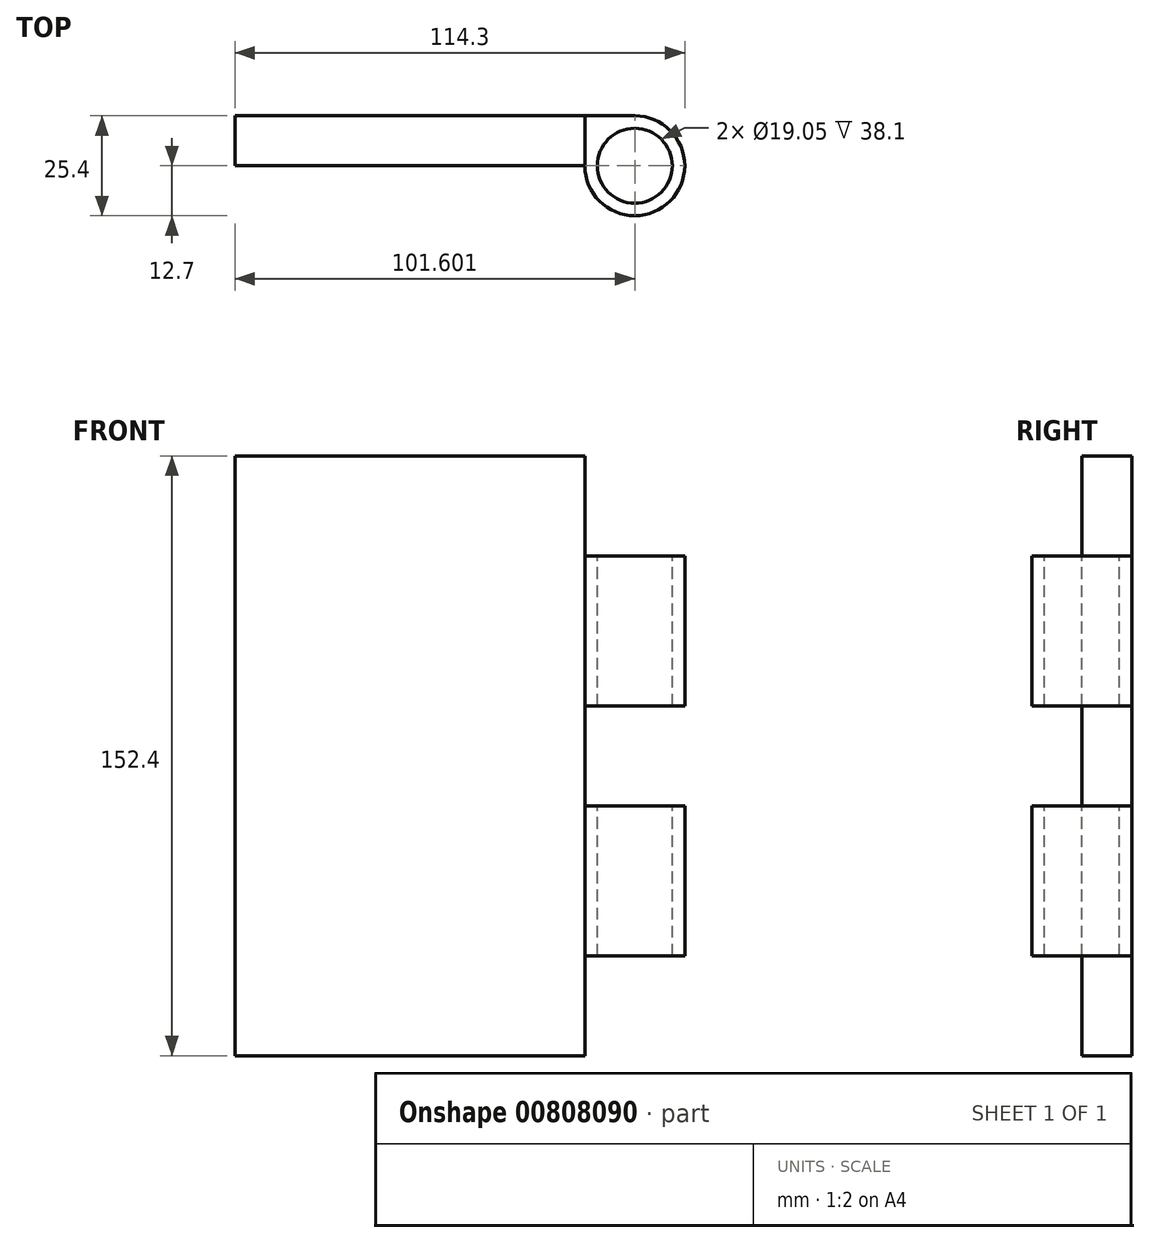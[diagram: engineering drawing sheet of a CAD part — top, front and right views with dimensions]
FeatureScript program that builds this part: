
annotation { "Feature Type Name" : "Feature", "Feature Type Description" : "" }
export const myFeature = defineFeature(function(context is Context, id is Id, definition is map)
    precondition{}
    {
        {
            var Q0;
            Q0=qCreatedBy(makeId("Front.planeOp"),FACE);
            var sketch = newSketch(context, id + "F0", { "sketchPlane" : qUnion([Q0])});
            skLineSegment(sketch, "E0.bottom", {"start": v(-39.5, 77.5) * mm, "end": v(62.1, 77.5) * mm});
            skLineSegment(sketch, "E0.top", {"start": v(-39.5, -74.9) * mm, "end": v(62.1, -74.9) * mm});
            skLineSegment(sketch, "E0.left", {"start": v(-39.5, 77.5) * mm, "end": v(-39.5, -74.9) * mm});
            skLineSegment(sketch, "E0.right", {"start": v(62.1, 77.5) * mm, "end": v(62.1, -74.9) * mm});
            skSolve(sketch);
        }
        {
            var Q0;
            Q0=makeQuery(id+"F0.imprint","IMPRINT",FACE,{"disambiguationData":[TD([[makeQuery(id+"F0.imprint","IMPRINT",EDGE,{"derivedFrom":sQuery(id+"F0.wireOp",EDGE,"E0.bottom")}),-1.0]])]});
            extrude(context, id + "F1", {"entities" : qUnion([Q0]), "depth" : 12.7 * mm, "offsetDistance" : 25.4 * mm});
        }
        {
            var Q0;
            Q0=makeQuery(id+"F1.opExtrude","SWEPT_FACE",FACE,{"disambiguationData":[OSD([sQuery(id+"F0.wireOp",EDGE,"E0.bottom")])]});
            var sketch = newSketch(context, id + "F2", { "sketchPlane" : qUnion([Q0])});
            skCircle(sketch, "E1", {"center": v(62.1, -12.7) * mm, "radius": 12.7 * mm});
            skSolve(sketch);
        }
        {
            var Q0;
            Q0=makeQuery(id+"F2.imprint","IMPRINT",FACE,{"disambiguationData":[TD([[makeQuery(id+"F2.imprint","IMPRINT",EDGE,{"derivedFrom":sQuery(id+"F2.wireOp",EDGE,"AtYBVnGq-jbLN-iIk4-UTEE-TkR76Q6qanXP")}),1.0]])]});
            var Q1;
            {var subQ1=sQuery(id+"F0.wireOp",EDGE,"E0.bottom");var subQ2=makeQuery(id+"F1.opExtrude","SWEPT_EDGE",EDGE,{"disambiguationData":[OSD([subQ1,sQuery(id+"F0.wireOp",EDGE,"E0.right")])]});Q1=makeQuery(id+"F2.imprint","IMPRINT",FACE,{"disambiguationData":[TD([[makeQuery(id+"F2.imprint","IMPRINT",EDGE,{"derivedFrom":subQ2}),-1.0]])]});}
            extrude(context, id + "F3", {"entities" : qUnion([Q0, Q1]), "operationType" : NewBodyOperationType.ADD, "oppositeDirection" : true, "depth" : 152.4 * mm, "offsetDistance" : 25.4 * mm});
        }
        {
            var Q0;
            {var subQ0=sQuery(id+"F0.wireOp",EDGE,"E0.bottom");Q0=makeQuery(id+"F3.boolean.opBoolean","MERGE",FACE,{"derivedFrom":[makeQuery(id+"F1.opExtrude","SWEPT_FACE",FACE,{"disambiguationData":[OSD([subQ0])]}),makeQuery(id+"F3.opExtrude","CAP_FACE",FACE,{"disambiguationData":[OSD([subQ0,sQuery(id+"F0.wireOp",EDGE,"E0.right"),sQuery(id+"F2.wireOp",EDGE,"AtYBVnGq-jbLN-iIk4-UTEE-TkR76Q6qanXP")])],"isStart":true})]});}
            var sketch = newSketch(context, id + "F4", { "sketchPlane" : qUnion([Q0])});
            skPoint(sketch, "E2", {"position": v(62.1, -12.7) * mm});
            skCircle(sketch, "E3", {"center": v(62.1, -12.7) * mm, "radius": 9.53 * mm});
            skSolve(sketch);
        }
        {
            var Q0;
            Q0=makeQuery(id+"F4.imprint","IMPRINT",FACE,{"disambiguationData":[TD([[makeQuery(id+"F4.imprint","IMPRINT",EDGE,{"derivedFrom":sQuery(id+"F4.wireOp",EDGE,"E3")}),1.0]])]});
            extrude(context, id + "F5", {"entities" : qUnion([Q0]), "operationType" : NewBodyOperationType.REMOVE, "endBound" : BoundingType.UP_TO_NEXT, "oppositeDirection" : true, "depth" : 25.4 * mm, "offsetDistance" : 25.4 * mm});
        }
        {
            var Q0;
            Q0=qCreatedBy(makeId("Front.planeOp"),FACE);
            cPlane(context, id + "F6", {"entities" : qUnion([Q0]), "cplaneType" : CPlaneType.OFFSET, "offset" : 25.4 * mm, "width" : 152.4 * mm, "height" : 152.4 * mm});
        }
        {
            var Q0;
            Q0=qCreatedBy(id+"F6.planeOp",FACE);
            var sketch = newSketch(context, id + "F7", { "sketchPlane" : qUnion([Q0])});
            skLineSegment(sketch, "E4.0", {"start": v(49.4, 77.5) * mm, "end": v(49.4, -74.9) * mm, "construction": true});
            skLineSegment(sketch, "E5.bottom", {"start": v(49.4, 77.5) * mm, "end": v(100.2, 77.5) * mm});
            skLineSegment(sketch, "E5.top", {"start": v(49.4, 52.1) * mm, "end": v(100.2, 52.1) * mm});
            skLineSegment(sketch, "E5.left", {"start": v(49.4, 77.5) * mm, "end": v(49.4, 52.1) * mm});
            skLineSegment(sketch, "E5.right", {"start": v(100.2, 77.5) * mm, "end": v(100.2, 52.1) * mm});
            skLineSegment(sketch, "E6.bottom", {"start": v(49.4, -49.5) * mm, "end": v(100.2, -49.5) * mm});
            skLineSegment(sketch, "E6.top", {"start": v(49.4, -74.9) * mm, "end": v(100.2, -74.9) * mm});
            skLineSegment(sketch, "E6.left", {"start": v(49.4, -49.5) * mm, "end": v(49.4, -74.9) * mm});
            skLineSegment(sketch, "E6.right", {"start": v(100.2, -49.5) * mm, "end": v(100.2, -74.9) * mm});
            skLineSegment(sketch, "E7.bottom", {"start": v(49.4, -11.4) * mm, "end": v(100.2, -11.4) * mm});
            skLineSegment(sketch, "E7.top", {"start": v(49.4, 14) * mm, "end": v(100.2, 14) * mm});
            skLineSegment(sketch, "E7.left", {"start": v(49.4, -11.4) * mm, "end": v(49.4, 14) * mm});
            skLineSegment(sketch, "E7.right", {"start": v(100.2, -11.4) * mm, "end": v(100.2, 14) * mm});
            skSolve(sketch);
        }
        {
            var Q0;
            Q0=makeQuery(id+"F7.imprint","IMPRINT",FACE,{"disambiguationData":[TD([[makeQuery(id+"F7.imprint","IMPRINT",EDGE,{"derivedFrom":sQuery(id+"F7.wireOp",EDGE,"E5.bottom")}),-1.0]])]});
            var Q1;
            Q1=makeQuery(id+"F7.imprint","IMPRINT",FACE,{"disambiguationData":[TD([[makeQuery(id+"F7.imprint","IMPRINT",EDGE,{"derivedFrom":sQuery(id+"F7.wireOp",EDGE,"E6.bottom")}),-1.0]])]});
            var Q2;
            Q2=makeQuery(id+"F7.imprint","IMPRINT",FACE,{"disambiguationData":[TD([[makeQuery(id+"F7.imprint","IMPRINT",EDGE,{"derivedFrom":sQuery(id+"F7.wireOp",EDGE,"E7.bottom")}),1.0]])]});
            extrude(context, id + "F8", {"entities" : qUnion([Q0, Q1, Q2]), "operationType" : NewBodyOperationType.REMOVE, "oppositeDirection" : true, "depth" : 50.8 * mm, "offsetDistance" : 25.4 * mm});
        }
    });
